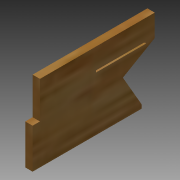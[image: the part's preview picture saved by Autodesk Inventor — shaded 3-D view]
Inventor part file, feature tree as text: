
AUTODESK INVENTOR PART (.ipt)
format: ipt  version: 2013 (Build 170138000, 138)  size: 103,424 bytes
history: native  units: in
note: dims shown in document units (in); Inventor stores cm internally (conversion verified against a paired STEP export)
features: extrude x1, sketch x1
ambient origin geometry x8: Origin, YZ Plane, XZ Plane, XY Plane, X Axis, Y Axis, Z Axis, Center Point
bodies: Solid1 (feature_tree)
feature tree (2):
  extrude  "Extrusion1"  TaperAngle=30.0deg  [1 undecoded]
  sketch  "Sketch1"  dims[d2=1.25in d4=30.0deg d6=2.6in d7=3.7in d8=1.275in d9=0.125in d10=1.7in d11=0.0625in d13=2.15in d14=0.25in d15=0.0in d16=0.25in d17=1.25in d18=1.9in]
note: 1 required parameter value undecoded (feature->parameter linkage not recoverable at this tier; creation-order binding heuristic only, values carry confidence <= 0.55)
